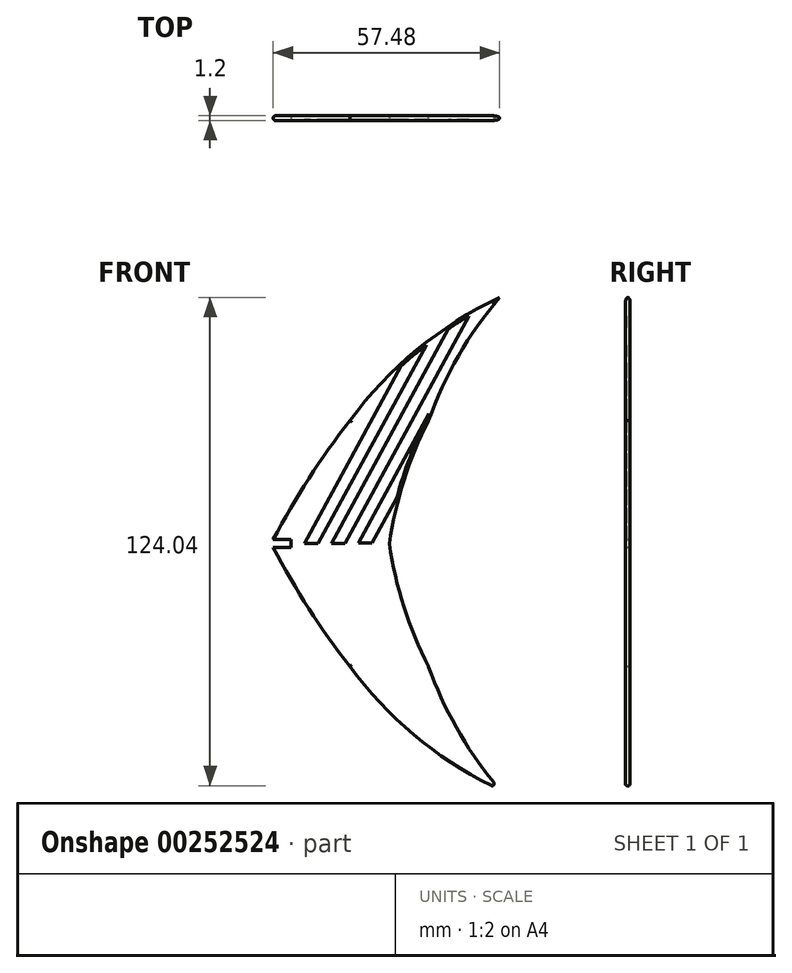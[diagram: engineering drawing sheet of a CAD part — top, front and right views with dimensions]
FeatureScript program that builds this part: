
annotation { "Feature Type Name" : "Feature", "Feature Type Description" : "" }
export const myFeature = defineFeature(function(context is Context, id is Id, definition is map)
    precondition{}
    {
        {
            var Q0;
            Q0=qCreatedBy(makeId("Front.planeOp"),FACE);
            var sketch = newSketch(context, id + "F0", { "sketchPlane" : qUnion([Q0])});
            skLineSegment(sketch, "E0", {"start": v(0, 0) * mm, "end": v(30, 0) * mm});
            skLineSegment(sketch, "E1", {"start": v(20, 31.25) * mm, "end": v(40, 31.25) * mm});
            skPoint(sketch, "E2", {"position": v(58, 62.5) * mm});
            skArc(sketch, "E3", {"start": v(20, 31.25) * mm, "mid": v(9.27, 16.09) * mm, "end": v(0, 0) * mm});
            skArc(sketch, "E4", {"start": v(58, 62.5) * mm, "mid": v(37.05, 49.25) * mm, "end": v(20, 31.25) * mm});
            skArc(sketch, "E5", {"start": v(58, 62.5) * mm, "mid": v(47.58, 47.7) * mm, "end": v(40, 31.25) * mm});
            skArc(sketch, "E6", {"start": v(40, 31.25) * mm, "mid": v(33.7, 16.04) * mm, "end": v(30, 0) * mm});
            skSolve(sketch);
        }
        {
            var Q0;
            Q0=qSketchRegion(id+"F0",true);
            extrude(context, id + "F1", {"entities" : qUnion([Q0]), "endBound" : BoundingType.SYMMETRIC, "depth" : 1.2 * mm});
        }
        {
            var Q0;
            Q0=makeQuery(id+"F1.opExtrude","SWEPT_BODY",BODY,{"disambiguationData":[OSD([sQuery(id+"F0.wireOp",EDGE,"E0"),sQuery(id+"F0.wireOp",EDGE,"E3"),sQuery(id+"F0.wireOp",EDGE,"E4"),sQuery(id+"F0.wireOp",EDGE,"E5"),sQuery(id+"F0.wireOp",EDGE,"E6")])]});
            var Q1;
            Q1=qCreatedBy(makeId("Top.planeOp"),FACE);
            mirror(context, id + "F2", {"operationType" : NewBodyOperationType.ADD, "entities" : qUnion([Q0]), "mirrorPlane" : qUnion([Q1])});
        }
        {
            var Q0;
            Q0=qCreatedBy(makeId("Front.planeOp"),FACE);
            var sketch = newSketch(context, id + "F3", { "sketchPlane" : qUnion([Q0])});
            skLineSegment(sketch, "E7.bottom", {"start": v(5, -1) * mm, "end": v(-5, -1) * mm});
            skLineSegment(sketch, "E7.top", {"start": v(5, 1) * mm, "end": v(-5, 1) * mm});
            skLineSegment(sketch, "E7.left", {"start": v(5, -1) * mm, "end": v(5, 1) * mm});
            skLineSegment(sketch, "E7.right", {"start": v(-5, -1) * mm, "end": v(-5, 1) * mm});
            skPoint(sketch, "E7.middle", {"position": v(0, 0) * mm});
            skSolve(sketch);
        }
        {
            var Q0;
            Q0=makeQuery(id+"F3.imprint","IMPRINT",FACE,{"disambiguationData":[TD([[makeQuery(id+"F3.imprint","IMPRINT",EDGE,{"derivedFrom":sQuery(id+"F3.wireOp",EDGE,"E7.bottom")}),-1.0]])]});
            extrude(context, id + "F4", {"entities" : qUnion([Q0]), "operationType" : NewBodyOperationType.REMOVE, "endBound" : BoundingType.SYMMETRIC, "oppositeDirection" : true, "depth" : 5 * mm});
        }
        {
            var Q0;
            Q0=makeQuery(id+"F1.opExtrude","CAP_EDGE",EDGE,{"disambiguationData":[OSD([sQuery(id+"F0.wireOp",EDGE,"E4")])],"isStart":false});
            var Q1;
            Q1=makeQuery(id+"F1.opExtrude","CAP_EDGE",EDGE,{"disambiguationData":[OSD([sQuery(id+"F0.wireOp",EDGE,"E4")])],"isStart":true});
            var Q2;
            Q2=makeQuery(id+"F1.opExtrude","CAP_EDGE",EDGE,{"disambiguationData":[OSD([sQuery(id+"F0.wireOp",EDGE,"E3")])],"isStart":false});
            var Q3;
            Q3=makeQuery(id+"F1.opExtrude","CAP_EDGE",EDGE,{"disambiguationData":[OSD([sQuery(id+"F0.wireOp",EDGE,"E3")])],"isStart":true});
            var Q4;
            Q4=makeQuery(id+"F1.opExtrude","CAP_EDGE",EDGE,{"disambiguationData":[OSD([sQuery(id+"F0.wireOp",EDGE,"E5")])],"isStart":false});
            var Q5;
            Q5=makeQuery(id+"F1.opExtrude","CAP_EDGE",EDGE,{"disambiguationData":[OSD([sQuery(id+"F0.wireOp",EDGE,"E5")])],"isStart":true});
            var Q6;
            Q6=makeQuery(id+"F1.opExtrude","CAP_EDGE",EDGE,{"disambiguationData":[OSD([sQuery(id+"F0.wireOp",EDGE,"E6")])],"isStart":false});
            var Q7;
            Q7=makeQuery(id+"F1.opExtrude","CAP_EDGE",EDGE,{"disambiguationData":[OSD([sQuery(id+"F0.wireOp",EDGE,"E6")])],"isStart":true});
            var Q8;
            Q8=makeQuery(id+"F2.opPattern","COPY",EDGE,{"derivedFrom":makeQuery(id+"F1.opExtrude","CAP_EDGE",EDGE,{"disambiguationData":[OSD([sQuery(id+"F0.wireOp",EDGE,"E3")])],"isStart":false}),"instanceName":"1"});
            var Q9;
            Q9=makeQuery(id+"F2.opPattern","COPY",EDGE,{"derivedFrom":makeQuery(id+"F1.opExtrude","CAP_EDGE",EDGE,{"disambiguationData":[OSD([sQuery(id+"F0.wireOp",EDGE,"E3")])],"isStart":true}),"instanceName":"1"});
            var Q10;
            Q10=makeQuery(id+"F2.opPattern","COPY",EDGE,{"derivedFrom":makeQuery(id+"F1.opExtrude","CAP_EDGE",EDGE,{"disambiguationData":[OSD([sQuery(id+"F0.wireOp",EDGE,"E4")])],"isStart":false}),"instanceName":"1"});
            var Q11;
            Q11=makeQuery(id+"F2.opPattern","COPY",EDGE,{"derivedFrom":makeQuery(id+"F1.opExtrude","CAP_EDGE",EDGE,{"disambiguationData":[OSD([sQuery(id+"F0.wireOp",EDGE,"E4")])],"isStart":true}),"instanceName":"1"});
            var Q12;
            Q12=makeQuery(id+"F2.opPattern","COPY",EDGE,{"derivedFrom":makeQuery(id+"F1.opExtrude","CAP_EDGE",EDGE,{"disambiguationData":[OSD([sQuery(id+"F0.wireOp",EDGE,"E6")])],"isStart":false}),"instanceName":"1"});
            var Q13;
            Q13=makeQuery(id+"F2.opPattern","COPY",FACE,{"derivedFrom":makeQuery(id+"F1.opExtrude","SWEPT_FACE",FACE,{"disambiguationData":[OSD([sQuery(id+"F0.wireOp",EDGE,"E6")])]}),"instanceName":"1"});
            var Q14;
            Q14=makeQuery(id+"F2.opPattern","COPY",EDGE,{"derivedFrom":makeQuery(id+"F1.opExtrude","CAP_EDGE",EDGE,{"disambiguationData":[OSD([sQuery(id+"F0.wireOp",EDGE,"E5")])],"isStart":false}),"instanceName":"1"});
            var Q15;
            Q15=makeQuery(id+"F2.opPattern","COPY",FACE,{"derivedFrom":makeQuery(id+"F1.opExtrude","SWEPT_FACE",FACE,{"disambiguationData":[OSD([sQuery(id+"F0.wireOp",EDGE,"E5")])]}),"instanceName":"1"});
            fillet(context, id + "F5", {"entities" : qUnion([Q0, Q1, Q2, Q3, Q4, Q5, Q6, Q7, Q8, Q9, Q10, Q11, Q12, Q13, Q14, Q15]), "radius" : 0.5 * mm, "tangentPropagation" : true, "allowEdgeOverflow" : false});
        }
        {
            var Q0;
            {var subQ0=makeQuery(id+"F1.opExtrude","CAP_FACE",FACE,{"disambiguationData":[OSD([sQuery(id+"F0.wireOp",EDGE,"E0"),sQuery(id+"F0.wireOp",EDGE,"E3"),sQuery(id+"F0.wireOp",EDGE,"E4"),sQuery(id+"F0.wireOp",EDGE,"E5"),sQuery(id+"F0.wireOp",EDGE,"E6")])],"isStart":false});Q0=makeQuery(id+"F2.boolean.opBoolean","MERGE",FACE,{"derivedFrom":[subQ0,makeQuery(id+"F2.opPattern","COPY",FACE,{"derivedFrom":subQ0,"instanceName":"1"})]});}
            var sketch = newSketch(context, id + "F6", { "sketchPlane" : qUnion([Q0])});
            skLineSegment(sketch, "E8", {"start": v(25, 36.63) * mm, "end": v(5, 0) * mm});
            skLineSegment(sketch, "E9", {"start": v(33.72, 46.35) * mm, "end": v(8.42, 0) * mm});
            skLineSegment(sketch, "E10", {"start": v(39.4, 50.5) * mm, "end": v(11.84, 0) * mm});
            skLineSegment(sketch, "E11", {"start": v(15.25, 0) * mm, "end": v(45.06, 54.6) * mm});
            skLineSegment(sketch, "E12", {"start": v(18.67, 0) * mm, "end": v(50.26, 57.86) * mm});
            skLineSegment(sketch, "E13", {"start": v(22.1, 0) * mm, "end": v(55.14, 60.54) * mm});
            skLineSegment(sketch, "E14", {"start": v(25.5, 0) * mm, "end": v(59.78, 62.77) * mm});
            skLineSegment(sketch, "E15", {"start": v(33.02, 45.06) * mm, "end": v(40.09, 51.74) * mm});
            skLineSegment(sketch, "E16", {"start": v(5, 0) * mm, "end": v(29.52, 0.15) * mm});
            skSolve(sketch);
        }
        {
            var Q0;
            {var subQ0=sQuery(id+"F6.wireOp",EDGE,"E8");Q0=makeQuery(id+"F6.imprint","IMPRINT",FACE,{"disambiguationData":[TD([[makeQuery(id+"F6.imprint","IMPRINT",EDGE,{"derivedFrom":subQ0}),-1.0]])]});}
            var Q1;
            {var subQ0=sQuery(id+"F6.wireOp",EDGE,"E15");Q1=makeQuery(id+"F6.imprint","IMPRINT",FACE,{"disambiguationData":[TD([[makeQuery(id+"F6.imprint","IMPRINT",EDGE,{"derivedFrom":subQ0}),-1.0]])]});}
            var Q2;
            {var subQ0=sQuery(id+"F6.wireOp",EDGE,"E11");var subQ5=sQuery(id+"F6.wireOp",EDGE,"E16");var subQ6=makeQuery(id+"F6.imprint","INTERSECT",VERTEX,{"derivedFrom":[subQ0,subQ5]});Q2=makeQuery(id+"F6.imprint","IMPRINT",FACE,{"disambiguationData":[TD([[makeQuery(id+"F6.imprint","IMPRINT",EDGE,{"disambiguationData":[TD([[subQ6,-1.0]])],"derivedFrom":subQ5}),1.0]])]});}
            var Q3;
            {var subQ0=sQuery(id+"F6.wireOp",EDGE,"E13");var subQ5=sQuery(id+"F6.wireOp",EDGE,"E16");var subQ6=makeQuery(id+"F6.imprint","INTERSECT",VERTEX,{"derivedFrom":[subQ0,subQ5]});Q3=makeQuery(id+"F6.imprint","IMPRINT",FACE,{"disambiguationData":[TD([[makeQuery(id+"F6.imprint","IMPRINT",EDGE,{"disambiguationData":[TD([[subQ6,-1.0]])],"derivedFrom":subQ5}),1.0]])]});}
            extrude(context, id + "F7", {"entities" : qUnion([Q0, Q1, Q2, Q3]), "operationType" : NewBodyOperationType.REMOVE, "oppositeDirection" : true, "depth" : 0.2 * mm});
        }
    });
